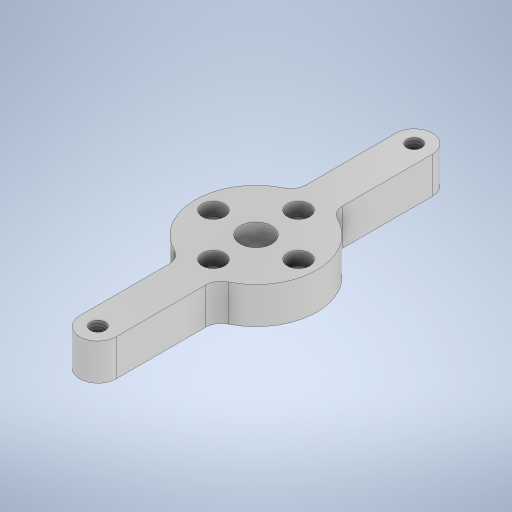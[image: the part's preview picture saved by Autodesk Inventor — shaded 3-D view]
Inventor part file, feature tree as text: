
AUTODESK INVENTOR PART (.ipt)
format: ipt  version: 2024.2 (Build 282272000, 272)  size: 313,344 bytes
history: native  units: mm
features: sketch x5, extrude x3, hole x2, projected_geometry x2, other x1
ambient origin geometry x8: Origin, YZ Plane, XZ Plane, XY Plane, X Axis, Y Axis, Z Axis, Center Point
bodies: Body1 (feature_tree)
feature tree (13):
  other  "솔리드1"
  extrude  "돌출1"  Depth=6.0mm TaperAngle=0.0deg
  hole  "구멍1"  [1 undecoded]
  extrude  "돌출2"  Depth=10.0mm
  hole  "구멍2"  [1 undecoded]
  extrude  "Extrusion3"  Depth=10.0mm
  sketch  "스케치1"
  sketch  "스케치2"
  sketch  "스케치3"
  projected_geometry  "투영된 루프1"
  sketch  "스케치4"
  projected_geometry  "투영된 루프2"
  sketch  "Sketch5"  dims[d0=20.0mm d1=6.0mm d2=0.0mm d3=14.0mm d4=2.1mm d5=4.0mm d6=3.7mm d7=2.2mm d8=90.0deg d9=4.0mm d10=0.0mm d11=4.0mm d12=4.0mm d13=26.0mm d14=26.0mm d15=3.0mm d19=5.0mm d20=3.0mm d21=6.0mm d22=0.0mm d23=2.459mm d24=3.0mm d25=4.0mm d26=2.2mm d27=90.0deg d28=3.0mm d29=0.0mm d30=5.2mm d31=10.0mm d32=0.0mm]
note: 2 required parameter values undecoded (feature->parameter linkage not recoverable at this tier; creation-order binding heuristic only, values carry confidence <= 0.55)
